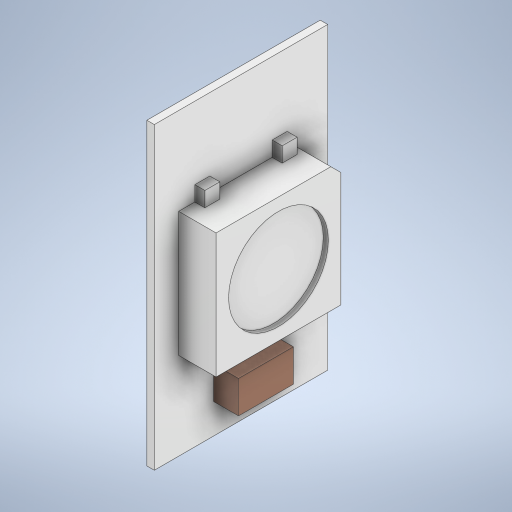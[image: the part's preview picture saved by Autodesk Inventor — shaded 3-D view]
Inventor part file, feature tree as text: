
AUTODESK INVENTOR PART (.ipt)
format: ipt  version: 2023 (Build 270158000, 158)  size: 320,512 bytes
history: native  units: mm
features: extrude x5, sketch x5, chamfer x1
ambient origin geometry x8: Origin, YZ Plane, XZ Plane, XY Plane, X Axis, Y Axis, Z Axis, Center Point
bodies: Solid1 (feature_tree)
feature tree (11):
  extrude  "Extrusion1"  Depth=6.95mm
  extrude  "Extrusion2"  Depth=5.0mm
  extrude  "Extrusion3"  Depth=1.5mm TaperAngle=0.0deg
  chamfer  "Chamfer1"  Distance=0.2mm
  extrude  "Extrusion4"  Depth=0.6mm
  extrude  "Extrusion5"  Depth=0.6mm
  sketch  "Sketch1"  dims[d0=12.0mm d1=6.95mm]
  sketch  "Sketch2"  dims[d2=0.3mm d3=0.0mm d4=5.0mm]
  sketch  "Sketch3"  dims[d5=5.0mm d6=1.5mm d7=0.0mm]
  sketch  "Sketch5"  dims[d8=4.0mm d9=0.2mm d10=0.0mm]
  sketch  "Sketch6"  dims[d11=0.4mm d12=2.0mm d13=45.0deg d14=0.6mm d15=0.6mm d16=2.5mm d17=0.4mm d18=0.0mm d20=2.2mm d21=1.2mm d22=1.0mm d23=0.0mm d24=2.5mm]
